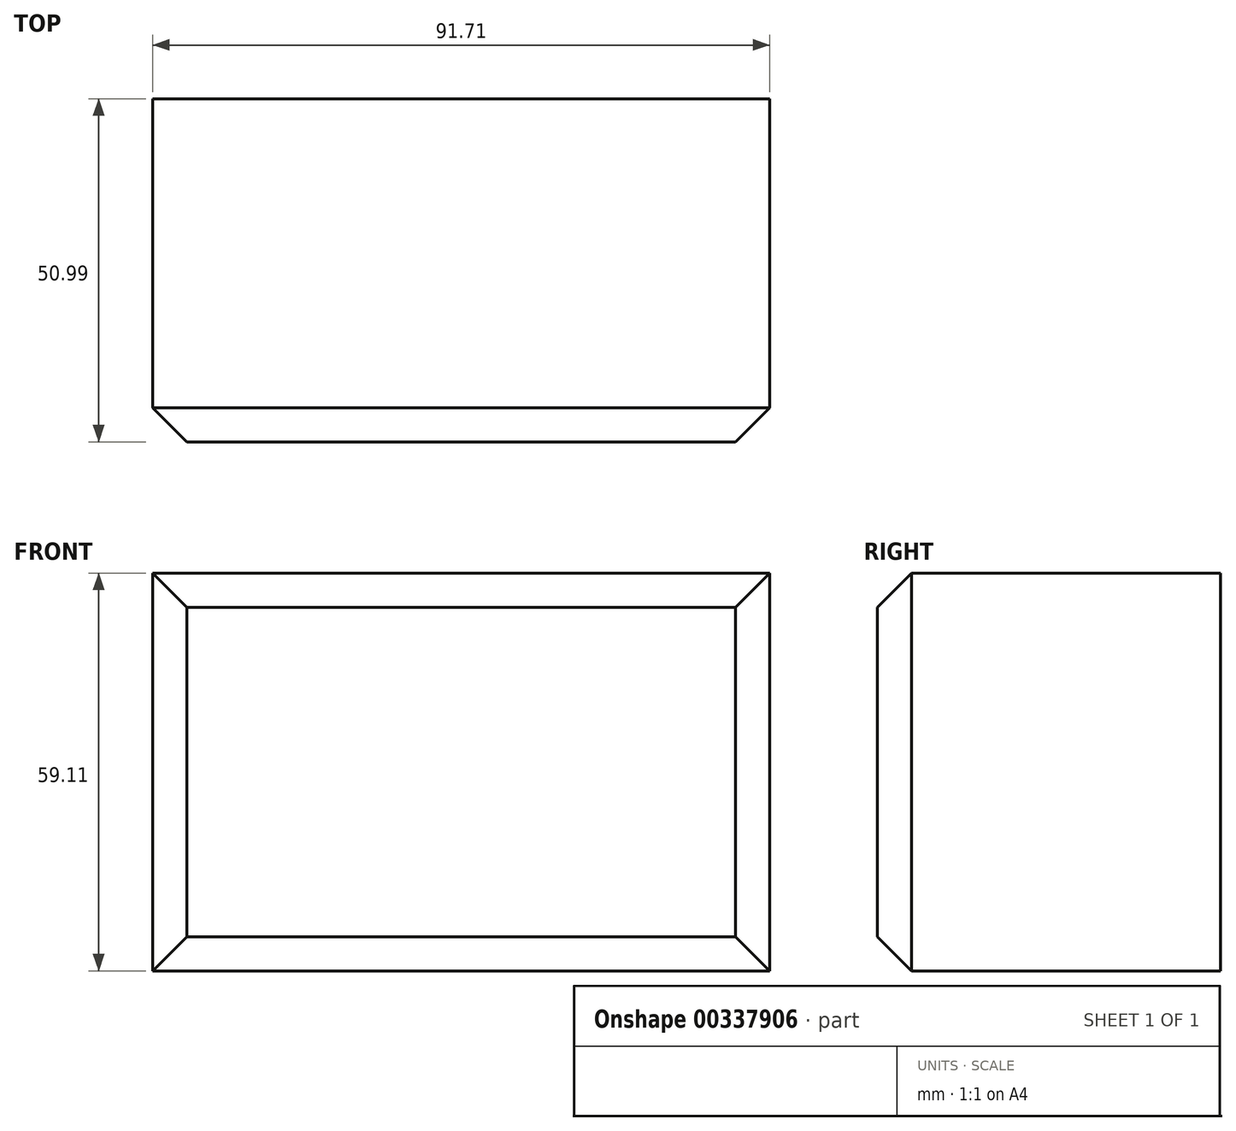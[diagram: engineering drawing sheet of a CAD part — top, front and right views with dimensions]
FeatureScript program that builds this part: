
annotation { "Feature Type Name" : "Feature", "Feature Type Description" : "" }
export const myFeature = defineFeature(function(context is Context, id is Id, definition is map)
    precondition{}
    {
        {
            var Q0;
            Q0=qCreatedBy(makeId("Right.planeOp"),FACE);
            var sketch = newSketch(context, id + "F0", { "sketchPlane" : qUnion([Q0])});
            skLineSegment(sketch, "E0.bottom", {"start": v(26.83, 0) * mm, "end": v(-24.16, 0) * mm});
            skLineSegment(sketch, "E0.top", {"start": v(26.83, 59.11) * mm, "end": v(-24.16, 59.11) * mm});
            skLineSegment(sketch, "E0.left", {"start": v(26.83, 0) * mm, "end": v(26.83, 59.11) * mm});
            skLineSegment(sketch, "E0.right", {"start": v(-24.16, 0) * mm, "end": v(-24.16, 59.11) * mm});
            skSolve(sketch);
        }
        {
            var Q0;
            Q0=makeQuery(id+"F0.imprint","IMPRINT",FACE,{"disambiguationData":[TD([[makeQuery(id+"F0.imprint","IMPRINT",EDGE,{"derivedFrom":sQuery(id+"F0.wireOp",EDGE,"E0.bottom")}),-1.0]])]});
            extrude(context, id + "F1", {"entities" : qUnion([Q0]), "depth" : 91.7 * mm});
        }
        {
            var Q0;
            Q0=makeQuery(id+"F1.opExtrude","SWEPT_FACE",FACE,{"disambiguationData":[OSD([sQuery(id+"F0.wireOp",EDGE,"E0.right")])]});
            chamfer(context, id + "F2", {"entities" : qUnion([Q0]), "width" : 5.08 * mm, "tangentPropagation" : true});
        }
        {
            var Q1;
            Q1=makeQuery(id+"F1.opExtrude","SWEPT_FACE",FACE,{"disambiguationData":[OSD([sQuery(id+"F0.wireOp",EDGE,"E0.top")])]});
            var Q2;
            Q2=makeQuery(id+"F1.opExtrude","SWEPT_FACE",FACE,{"disambiguationData":[OSD([sQuery(id+"F0.wireOp",EDGE,"E0.right")])]});
            loft(context, id + "F3", {"operationType" : NewBodyOperationType.ADD, "sheetProfilesArray" : [{ "sheetProfileEntities" : qUnion([Q1]) }, { "sheetProfileEntities" : qUnion([Q2]) }]});
        }
    });
